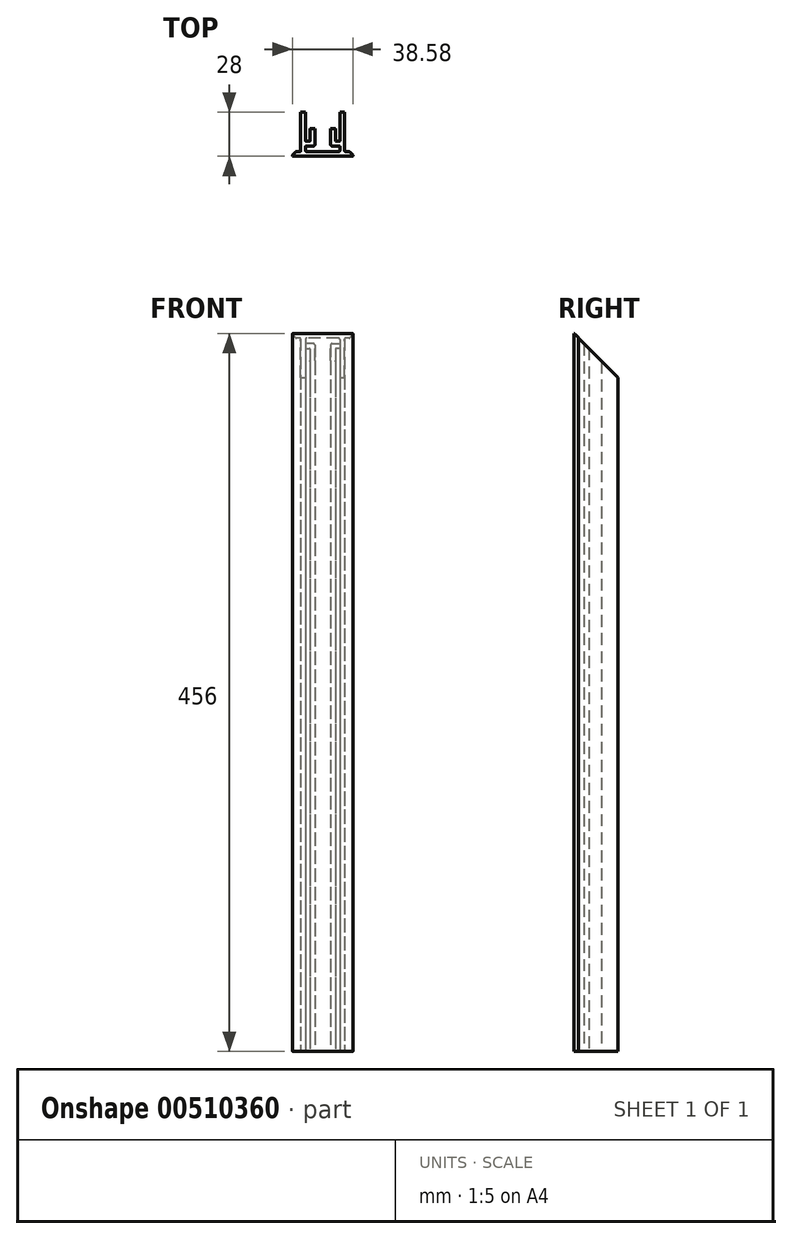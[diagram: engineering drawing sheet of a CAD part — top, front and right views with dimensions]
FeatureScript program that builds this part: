
annotation { "Feature Type Name" : "Feature", "Feature Type Description" : "" }
export const myFeature = defineFeature(function(context is Context, id is Id, definition is map)
    precondition{}
    {
        {
            var Q0;
            Q0=qCreatedBy(makeId("Top.planeOp"),FACE);
            var sketch = newSketch(context, id + "F0", { "sketchPlane" : qUnion([Q0])});
            skLineSegment(sketch, "E0", {"start": v(0, 37.2) * mm, "end": v(0, -38.8) * mm, "construction": true});
            skLineSegment(sketch, "E1", {"start": v(-30.9, 0) * mm, "end": v(40.1, 0) * mm, "construction": true});
            skLineSegment(sketch, "E2.bottom", {"start": v(-17, 0.5) * mm, "end": v(17, 0.5) * mm});
            skLineSegment(sketch, "E2.top", {"start": v(-20, -2.5) * mm, "end": v(20, -2.5) * mm});
            skLineSegment(sketch, "E3", {"start": v(-20, -2.5) * mm, "end": v(-17, 0.5) * mm});
            skLineSegment(sketch, "E4.MirrorCS", {"start": v(20, -2.5) * mm, "end": v(17, 0.5) * mm});
            skLineSegment(sketch, "E5", {"start": v(14, 0.5) * mm, "end": v(14, 25.5) * mm});
            skLineSegment(sketch, "E6", {"start": v(14, 25.5) * mm, "end": v(11, 25.5) * mm});
            skLineSegment(sketch, "E7", {"start": v(11, 25.5) * mm, "end": v(11, 0.5) * mm});
            skLineSegment(sketch, "E8.MirrorCS", {"start": v(-14, 25.5) * mm, "end": v(-11, 25.5) * mm});
            skLineSegment(sketch, "E9.MirrorCS", {"start": v(-14, 0.5) * mm, "end": v(-14, 25.5) * mm});
            skLineSegment(sketch, "E10.MirrorCS", {"start": v(-11, 25.5) * mm, "end": v(-11, 0.5) * mm});
            skLineSegment(sketch, "E11", {"start": v(11, 4) * mm, "end": v(5, 4) * mm});
            skLineSegment(sketch, "E12", {"start": v(5, 4) * mm, "end": v(5, 7) * mm});
            skLineSegment(sketch, "E13", {"start": v(5, 7) * mm, "end": v(5, 15) * mm});
            skLineSegment(sketch, "E14", {"start": v(5, 15) * mm, "end": v(8, 15) * mm});
            skLineSegment(sketch, "E15", {"start": v(8, 15) * mm, "end": v(8, 7) * mm});
            skLineSegment(sketch, "E16", {"start": v(8, 7) * mm, "end": v(11, 7) * mm});
            skLineSegment(sketch, "E17.MirrorCS", {"start": v(-5, 15) * mm, "end": v(-8, 15) * mm});
            skLineSegment(sketch, "E18.MirrorCS", {"start": v(-5, 7) * mm, "end": v(-5, 15) * mm});
            skLineSegment(sketch, "E19.MirrorCS", {"start": v(-11, 4) * mm, "end": v(-5, 4) * mm});
            skLineSegment(sketch, "E20.MirrorCS", {"start": v(-8, 7) * mm, "end": v(-11, 7) * mm});
            skLineSegment(sketch, "E21.MirrorCS", {"start": v(-8, 15) * mm, "end": v(-8, 7) * mm});
            skLineSegment(sketch, "E22.MirrorCS", {"start": v(-5, 4) * mm, "end": v(-5, 7) * mm});
            skSolve(sketch);
        }
        {
            var Q0;
            Q0=qSketchRegion(id+"F0",true);
            extrude(context, id + "F1", {"entities" : qUnion([Q0]), "depth" : 456 * mm, "symmetric" : true});
        }
        {
            var Q0;
            Q0=qCreatedBy(makeId("Right.planeOp"),FACE);
            var sketch = newSketch(context, id + "F2", { "sketchPlane" : qUnion([Q0])});
            skLineSegment(sketch, "E23.0", {"start": v(0.5, 228) * mm, "end": v(25.5, 228) * mm});
            skLineSegment(sketch, "E23.1", {"start": v(-2.5, 228) * mm, "end": v(0.5, 228) * mm});
            skLineSegment(sketch, "E24", {"start": v(-2.5, 228) * mm, "end": v(25.5, 200) * mm});
            skLineSegment(sketch, "E25", {"start": v(25.5, 200) * mm, "end": v(25.5, 228) * mm});
            skSolve(sketch);
        }
        {
            var Q0;
            Q0=qSketchRegion(id+"F2",true);
            extrude(context, id + "F3", {"entities" : qUnion([Q0]), "operationType" : NewBodyOperationType.REMOVE, "oppositeDirection" : true, "depth" : 60 * mm, "symmetric" : true});
        }
        {
            var Q0;
            Q0=makeQuery(id+"F1.opExtrude","SWEPT_EDGE",EDGE,{"disambiguationData":[OSD([sQuery(id+"F0.wireOp",EDGE,"E2.bottom"),sQuery(id+"F0.wireOp",EDGE,"E4.MirrorCS")])]});
            var Q1;
            {var subQ0=sQuery(id+"F2.wireOp",EDGE,"E24");Q1=makeQuery(id+"F3.boolean.opBoolean","COPY",EDGE,{"disambiguationData":[topologyDisambiguationEdgeConnected([makeQuery(id+"F1.opExtrude","SWEPT_FACE",FACE,{"disambiguationData":[OSD([sQuery(id+"F0.wireOp",EDGE,"E6")])]})])],"derivedFrom":makeQuery(id+"F3.opExtrude","SWEPT_EDGE",EDGE,{"disambiguationData":[OSD([subQ0,sQuery(id+"F2.wireOp",EDGE,"E25")])]})});}
            var Q2;
            Q2=makeQuery(id+"F1.opExtrude","SWEPT_EDGE",EDGE,{"disambiguationData":[OSD([sQuery(id+"F0.wireOp",EDGE,"E2.bottom"),sQuery(id+"F0.wireOp",EDGE,"E10.MirrorCS")])]});
            var Q3;
            {var subQ0=sQuery(id+"F2.wireOp",EDGE,"E24");Q3=makeQuery(id+"F3.boolean.opBoolean","COPY",EDGE,{"disambiguationData":[topologyDisambiguationEdgeConnected([makeQuery(id+"F1.opExtrude","SWEPT_FACE",FACE,{"disambiguationData":[OSD([sQuery(id+"F0.wireOp",EDGE,"E8.MirrorCS")])]})])],"derivedFrom":makeQuery(id+"F3.opExtrude","SWEPT_EDGE",EDGE,{"disambiguationData":[OSD([subQ0,sQuery(id+"F2.wireOp",EDGE,"E25")])]})});}
            var Q4;
            Q4=makeQuery(id+"F1.opExtrude","SWEPT_EDGE",EDGE,{"disambiguationData":[OSD([sQuery(id+"F0.wireOp",EDGE,"E2.bottom"),sQuery(id+"F0.wireOp",EDGE,"E3")])]});
            var Q5;
            Q5=makeQuery(id+"F1.opExtrude","SWEPT_EDGE",EDGE,{"disambiguationData":[OSD([sQuery(id+"F0.wireOp",EDGE,"E2.bottom"),sQuery(id+"F0.wireOp",EDGE,"E7")])]});
            var Q6;
            {var subQ0=sQuery(id+"F2.wireOp",EDGE,"E24");Q6=makeQuery(id+"FuO8uSxEj4nSnSF_1.1.F3.boolean.opBoolean","COPY",EDGE,{"disambiguationData":[topologyDisambiguationEdgeConnected([makeQuery(id+"F1.opExtrude","SWEPT_FACE",FACE,{"disambiguationData":[OSD([sQuery(id+"F0.wireOp",EDGE,"E8.MirrorCS")])]})])],"derivedFrom":makeQuery(id+"FuO8uSxEj4nSnSF_1.1.F3.opExtrude","SWEPT_EDGE",EDGE,{"disambiguationData":[OSD([subQ0,sQuery(id+"F2.wireOp",EDGE,"E25")])]})});}
            var Q7;
            {var subQ0=sQuery(id+"F2.wireOp",EDGE,"E24");Q7=makeQuery(id+"FuO8uSxEj4nSnSF_1.1.F3.boolean.opBoolean","COPY",EDGE,{"disambiguationData":[topologyDisambiguationEdgeConnected([makeQuery(id+"F1.opExtrude","SWEPT_FACE",FACE,{"disambiguationData":[OSD([sQuery(id+"F0.wireOp",EDGE,"E6")])]})])],"derivedFrom":makeQuery(id+"FuO8uSxEj4nSnSF_1.1.F3.opExtrude","SWEPT_EDGE",EDGE,{"disambiguationData":[OSD([subQ0,sQuery(id+"F2.wireOp",EDGE,"E25")])]})});}
            fillet(context, id + "F4", {"entities" : qUnion([Q0, Q1, Q2, Q3, Q4, Q5, Q6, Q7]), "radius" : 1 * mm, "tangentPropagation" : true, "allowEdgeOverflow" : false});
        }
        {
            var Q0;
            Q0=makeQuery(id+"F3.boolean.opBoolean","INTERSECT",EDGE,{"derivedFrom":[makeQuery(id+"F1.opExtrude","SWEPT_FACE",FACE,{"disambiguationData":[OSD([sQuery(id+"F0.wireOp",EDGE,"E17.MirrorCS")])]}),makeQuery(id+"F3.opExtrude","SWEPT_FACE",FACE,{"disambiguationData":[OSD([sQuery(id+"F2.wireOp",EDGE,"E24")])]})]});
            var Q1;
            Q1=makeQuery(id+"F3.boolean.opBoolean","INTERSECT",EDGE,{"derivedFrom":[makeQuery(id+"F1.opExtrude","SWEPT_FACE",FACE,{"disambiguationData":[OSD([sQuery(id+"F0.wireOp",EDGE,"E14")])]}),makeQuery(id+"F3.opExtrude","SWEPT_FACE",FACE,{"disambiguationData":[OSD([sQuery(id+"F2.wireOp",EDGE,"E24")])]})]});
            var Q2;
            Q2=makeQuery(id+"FuO8uSxEj4nSnSF_1.1.F3.boolean.opBoolean","INTERSECT",EDGE,{"derivedFrom":[makeQuery(id+"F1.opExtrude","SWEPT_FACE",FACE,{"disambiguationData":[OSD([sQuery(id+"F0.wireOp",EDGE,"E14")])]}),makeQuery(id+"FuO8uSxEj4nSnSF_1.1.F3.opExtrude","SWEPT_FACE",FACE,{"disambiguationData":[OSD([sQuery(id+"F2.wireOp",EDGE,"E24")])]})]});
            var Q3;
            Q3=makeQuery(id+"FuO8uSxEj4nSnSF_1.1.F3.boolean.opBoolean","INTERSECT",EDGE,{"derivedFrom":[makeQuery(id+"F1.opExtrude","SWEPT_FACE",FACE,{"disambiguationData":[OSD([sQuery(id+"F0.wireOp",EDGE,"E17.MirrorCS")])]}),makeQuery(id+"FuO8uSxEj4nSnSF_1.1.F3.opExtrude","SWEPT_FACE",FACE,{"disambiguationData":[OSD([sQuery(id+"F2.wireOp",EDGE,"E24")])]})]});
            var Q4;
            Q4=makeQuery(id+"F1.opExtrude","SWEPT_EDGE",EDGE,{"disambiguationData":[OSD([sQuery(id+"F0.wireOp",EDGE,"E19.MirrorCS"),sQuery(id+"F0.wireOp",EDGE,"E22.MirrorCS")])]});
            var Q5;
            Q5=makeQuery(id+"F1.opExtrude","SWEPT_EDGE",EDGE,{"disambiguationData":[OSD([sQuery(id+"F0.wireOp",EDGE,"E11"),sQuery(id+"F0.wireOp",EDGE,"E12")])]});
            fillet(context, id + "F5", {"entities" : qUnion([Q0, Q1, Q2, Q3, Q4, Q5]), "radius" : 1 * mm, "tangentPropagation" : true, "allowEdgeOverflow" : false});
        }
        {
            var Q0;
            Q0=makeQuery(id+"F1.opExtrude","SWEPT_EDGE",EDGE,{"disambiguationData":[OSD([sQuery(id+"F0.wireOp",EDGE,"E15"),sQuery(id+"F0.wireOp",EDGE,"E16")])]});
            var Q1;
            Q1=makeQuery(id+"F1.opExtrude","SWEPT_EDGE",EDGE,{"disambiguationData":[OSD([sQuery(id+"F0.wireOp",EDGE,"E10.MirrorCS"),sQuery(id+"F0.wireOp",EDGE,"E20.MirrorCS")])]});
            var Q2;
            Q2=makeQuery(id+"F1.opExtrude","SWEPT_EDGE",EDGE,{"disambiguationData":[OSD([sQuery(id+"F0.wireOp",EDGE,"E10.MirrorCS"),sQuery(id+"F0.wireOp",EDGE,"E19.MirrorCS")])]});
            var Q3;
            Q3=makeQuery(id+"F1.opExtrude","SWEPT_EDGE",EDGE,{"disambiguationData":[OSD([sQuery(id+"F0.wireOp",EDGE,"E7"),sQuery(id+"F0.wireOp",EDGE,"E11")])]});
            var Q4;
            Q4=makeQuery(id+"F1.opExtrude","SWEPT_EDGE",EDGE,{"disambiguationData":[OSD([sQuery(id+"F0.wireOp",EDGE,"E7"),sQuery(id+"F0.wireOp",EDGE,"E16")])]});
            var Q5;
            Q5=makeQuery(id+"F1.opExtrude","SWEPT_EDGE",EDGE,{"disambiguationData":[OSD([sQuery(id+"F0.wireOp",EDGE,"E20.MirrorCS"),sQuery(id+"F0.wireOp",EDGE,"E21.MirrorCS")])]});
            fillet(context, id + "F6", {"entities" : qUnion([Q0, Q1, Q2, Q3, Q4, Q5]), "radius" : 0.5 * mm, "tangentPropagation" : true, "allowEdgeOverflow" : false});
        }
        {
            var Q0;
            Q0=makeQuery(id+"F1.opExtrude","SWEPT_EDGE",EDGE,{"disambiguationData":[OSD([sQuery(id+"F0.wireOp",EDGE,"E2.top"),sQuery(id+"F0.wireOp",EDGE,"E3")])]});
            var Q1;
            Q1=makeQuery(id+"F1.opExtrude","SWEPT_EDGE",EDGE,{"disambiguationData":[OSD([sQuery(id+"F0.wireOp",EDGE,"E2.top"),sQuery(id+"F0.wireOp",EDGE,"E4.MirrorCS")])]});
            var Q2;
            Q2=makeQuery(id+"F1.opExtrude","SWEPT_EDGE",EDGE,{"disambiguationData":[OSD([sQuery(id+"F0.wireOp",EDGE,"E2.bottom"),sQuery(id+"F0.wireOp",EDGE,"E5")])]});
            var Q3;
            Q3=makeQuery(id+"F1.opExtrude","SWEPT_EDGE",EDGE,{"disambiguationData":[OSD([sQuery(id+"F0.wireOp",EDGE,"E2.bottom"),sQuery(id+"F0.wireOp",EDGE,"E9.MirrorCS")])]});
            fillet(context, id + "F7", {"entities" : qUnion([Q0, Q1, Q2, Q3]), "radius" : 0.5 * mm, "tangentPropagation" : true, "allowEdgeOverflow" : false});
        }
    });
